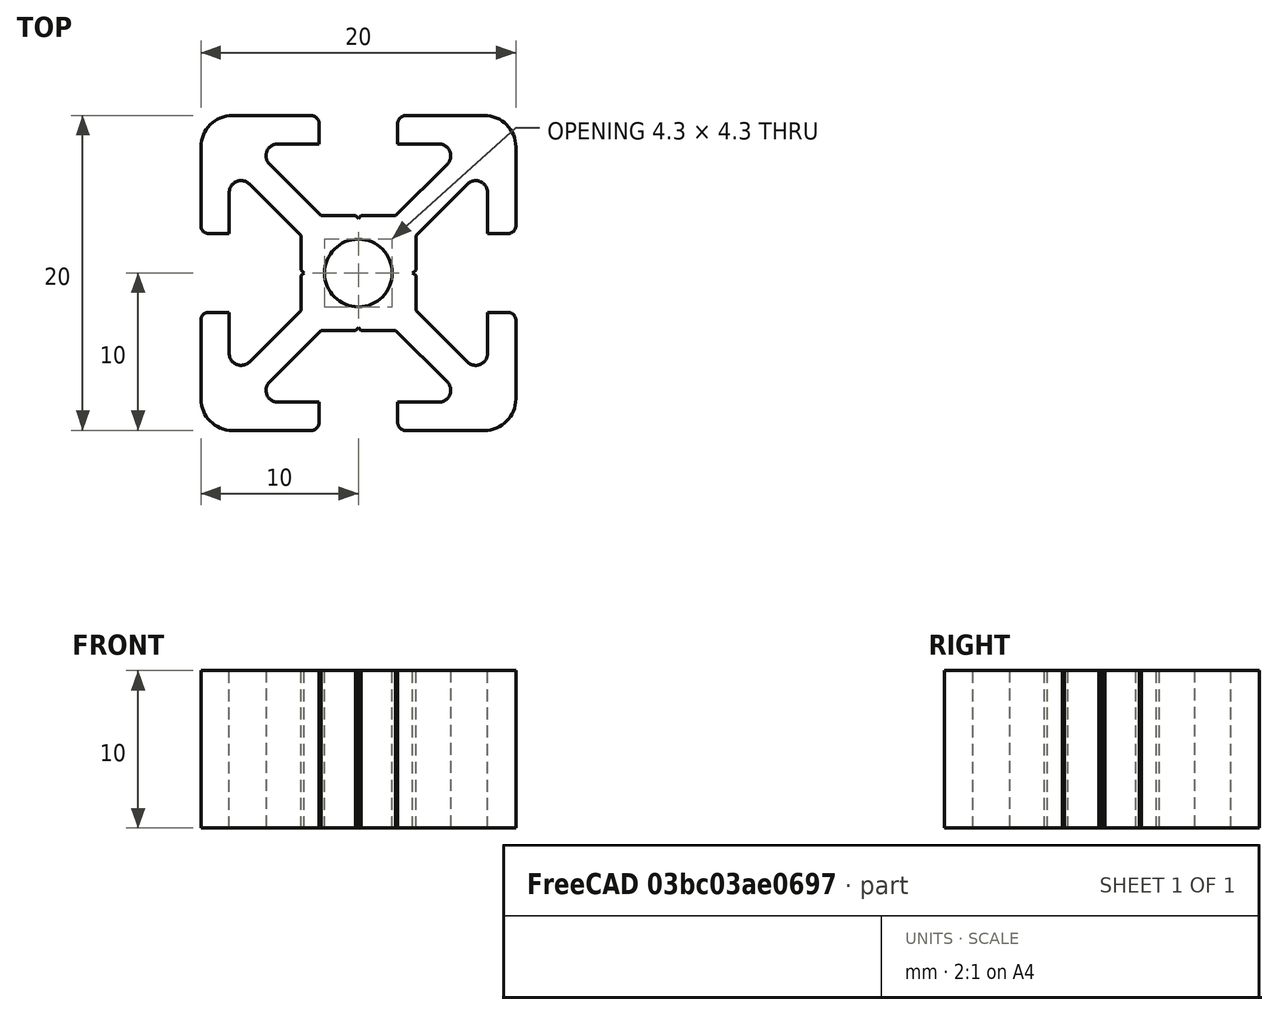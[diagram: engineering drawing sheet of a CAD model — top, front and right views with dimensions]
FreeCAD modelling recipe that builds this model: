
FCSTD DOCUMENT  (FreeCAD 0.18R)
Label: Profile-20x20-I-Type_Slot5
Comment: Item Compatible Profile\nLook for ISP5-L20
License: All rights reserved
LicenseURL: http://en.wikipedia.org/wiki/All_rights_reserved
objects: Sketcher::SketchObject×1, PartDesign::Pad×1, PartDesign::Body×1
note: 4 computed .brp shape members not serialized (recipe doc carries the construction recipe); baked Part::Feature solids carry a one-line shape summary decoded from their .brp

FEATURE [Sketcher::SketchObject] CopySketch029  label="ISP5-L20-Profile"
  MapMode = 5
  sketch-geometry (92):
    g0: LineSegment StartX=-2.37721 StartY=3.65 StartZ=0 EndX=-5.64688 EndY=6.91967 EndZ=0
    g1: LineSegment StartX=-5.11655 StartY=8.2 StartZ=0 EndX=-2.5 EndY=8.2 EndZ=0
    g2: LineSegment StartX=-3 StartY=10 StartZ=0 EndX=-8 EndY=10 EndZ=0
    g3: LineSegment StartX=-10 StartY=8 StartZ=0 EndX=-10 EndY=3 EndZ=0
    g4: LineSegment StartX=-9.5 StartY=2.5 StartZ=0 EndX=-8.2 EndY=2.5 EndZ=0
    g5: LineSegment StartX=-8.2 StartY=2.5 StartZ=0 EndX=-8.2 EndY=5.11655 EndZ=0
    g6: LineSegment StartX=-6.91967 StartY=5.64688 StartZ=0 EndX=-3.65 EndY=2.37721 EndZ=0
    g7: LineSegment StartX=-3.65 StartY=2.37721 StartZ=0 EndX=-3.65 EndY=0.177208 EndZ=0
    g8: LineSegment StartX=-0.177208 StartY=3.65 StartZ=0 EndX=-2.37721 EndY=3.65 EndZ=0
    g9: LineSegment StartX=-2.5 StartY=9.5 StartZ=0 EndX=-2.5 EndY=8.2 EndZ=0
    g10: LineSegment [constr] StartX=-8 StartY=8 StartZ=0 EndX=-9e-16 EndY=0 EndZ=0
    g11: LineSegment [constr] StartX=-3.65 StartY=2.37721 StartZ=0 EndX=-2.37721 EndY=3.65 EndZ=0
    g12: ArcOfCircle CenterX=-8 CenterY=8 CenterZ=0 NormalX=0 NormalY=0 NormalZ=1 AngleXU=0 Radius=2 StartAngle=1.5708 EndAngle=3.14159
    g13: ArcOfCircle CenterX=-3 CenterY=9.5 CenterZ=0 NormalX=0 NormalY=0 NormalZ=1 AngleXU=0 Radius=0.5 StartAngle=7e-16 EndAngle=1.5708
    g14: ArcOfCircle CenterX=-9.5 CenterY=3 CenterZ=0 NormalX=0 NormalY=0 NormalZ=1 AngleXU=0 Radius=0.5 StartAngle=3.14159 EndAngle=4.71239
    g15: ArcOfCircle CenterX=-5.11655 CenterY=7.45 CenterZ=0 NormalX=0 NormalY=0 NormalZ=1 AngleXU=0 Radius=0.75 StartAngle=1.5708 EndAngle=3.92699
    g16: ArcOfCircle CenterX=-7.45 CenterY=5.11655 CenterZ=0 NormalX=0 NormalY=0 NormalZ=1 AngleXU=0 Radius=0.75 StartAngle=0.785398 EndAngle=3.14159
    g17: LineSegment [constr] StartX=-5.11655 StartY=7.45 StartZ=0 EndX=-7.45 EndY=5.11655 EndZ=0
    g18: ArcOfCircle CenterX=-9e-16 CenterY=0 CenterZ=0 NormalX=0 NormalY=0 NormalZ=1 AngleXU=0 Radius=2.15 StartAngle=1.5708 EndAngle=3.14159
    g19: LineSegment StartX=1e-16 StartY=3.45 StartZ=0 EndX=1e-16 EndY=2.15 EndZ=0
    g20: LineSegment StartX=-3.45 StartY=3e-16 StartZ=0 EndX=-2.15 EndY=3e-16 EndZ=0
    g21: LineSegment StartX=-0.177208 StartY=3.65 StartZ=0 EndX=1e-16 EndY=3.45 EndZ=0
    g22: LineSegment StartX=-3.65 StartY=0.177208 StartZ=0 EndX=-3.45 EndY=3e-16 EndZ=0
    g23: LineSegment StartX=2.37721 StartY=3.65 StartZ=0 EndX=5.64688 EndY=6.91967 EndZ=0
    g24: LineSegment StartX=5.11655 StartY=8.2 StartZ=0 EndX=2.5 EndY=8.2 EndZ=0
    g25: LineSegment StartX=3 StartY=10 StartZ=0 EndX=8 EndY=10 EndZ=0
    g26: LineSegment StartX=10 StartY=8 StartZ=0 EndX=10 EndY=3 EndZ=0
    g27: LineSegment StartX=9.5 StartY=2.5 StartZ=0 EndX=8.2 EndY=2.5 EndZ=0
    g28: LineSegment StartX=8.2 StartY=2.5 StartZ=0 EndX=8.2 EndY=5.11655 EndZ=0
    g29: LineSegment StartX=6.91967 StartY=5.64688 StartZ=0 EndX=3.65 EndY=2.37721 EndZ=0
    g30: LineSegment StartX=3.65 StartY=2.37721 StartZ=0 EndX=3.65 EndY=0.177208 EndZ=0
    g31: LineSegment StartX=0.177208 StartY=3.65 StartZ=0 EndX=2.37721 EndY=3.65 EndZ=0
    g32: LineSegment StartX=2.5 StartY=9.5 StartZ=0 EndX=2.5 EndY=8.2 EndZ=0
    g33: LineSegment [constr] StartX=8 StartY=8 StartZ=0 EndX=9e-16 EndY=0 EndZ=0
    g34: LineSegment [constr] StartX=3.65 StartY=2.37721 StartZ=0 EndX=2.37721 EndY=3.65 EndZ=0
    g35: ArcOfCircle CenterX=8 CenterY=8 CenterZ=0 NormalX=0 NormalY=0 NormalZ=1 AngleXU=0 Radius=2 StartAngle=0 EndAngle=1.5708
    g36: ArcOfCircle CenterX=3 CenterY=9.5 CenterZ=0 NormalX=0 NormalY=0 NormalZ=1 AngleXU=0 Radius=0.5 StartAngle=1.5708 EndAngle=3.14159
    g37: ArcOfCircle CenterX=9.5 CenterY=3 CenterZ=0 NormalX=0 NormalY=0 NormalZ=1 AngleXU=0 Radius=0.5 StartAngle=4.71239 EndAngle=6.28319
    g38: ArcOfCircle CenterX=5.11655 CenterY=7.45 CenterZ=0 NormalX=0 NormalY=0 NormalZ=1 AngleXU=0 Radius=0.75 StartAngle=5.49779 EndAngle=7.85398
    g39: ArcOfCircle CenterX=7.45 CenterY=5.11655 CenterZ=0 NormalX=0 NormalY=0 NormalZ=1 AngleXU=0 Radius=0.75 StartAngle=0 EndAngle=2.35619
    g40: LineSegment [constr] StartX=5.11655 StartY=7.45 StartZ=0 EndX=7.45 EndY=5.11655 EndZ=0
    g41: ArcOfCircle CenterX=9e-16 CenterY=0 CenterZ=0 NormalX=0 NormalY=0 NormalZ=1 AngleXU=0 Radius=2.15 StartAngle=1e-16 EndAngle=1.5708
    g42: LineSegment StartX=5e-16 StartY=3.45 StartZ=0 EndX=5e-16 EndY=2.15 EndZ=0
    g43: LineSegment StartX=3.45 StartY=3e-16 StartZ=0 EndX=2.15 EndY=3e-16 EndZ=0
    g44: LineSegment StartX=0.177208 StartY=3.65 StartZ=0 EndX=5e-16 EndY=3.45 EndZ=0
    g45: LineSegment StartX=3.65 StartY=0.177208 StartZ=0 EndX=3.45 EndY=3e-16 EndZ=0
    g46: LineSegment StartX=-2.37721 StartY=-3.65 StartZ=0 EndX=-5.64688 EndY=-6.91967 EndZ=0
    g47: LineSegment StartX=-5.11655 StartY=-8.2 StartZ=0 EndX=-2.5 EndY=-8.2 EndZ=0
    g48: LineSegment StartX=-3 StartY=-10 StartZ=0 EndX=-8 EndY=-10 EndZ=0
    g49: LineSegment StartX=-10 StartY=-8 StartZ=0 EndX=-10 EndY=-3 EndZ=0
    g50: LineSegment StartX=-9.5 StartY=-2.5 StartZ=0 EndX=-8.2 EndY=-2.5 EndZ=0
    g51: LineSegment StartX=-8.2 StartY=-2.5 StartZ=0 EndX=-8.2 EndY=-5.11655 EndZ=0
    g52: LineSegment StartX=-6.91967 StartY=-5.64688 StartZ=0 EndX=-3.65 EndY=-2.37721 EndZ=0
    g53: LineSegment StartX=-3.65 StartY=-2.37721 StartZ=0 EndX=-3.65 EndY=-0.177208 EndZ=0
    g54: LineSegment StartX=-0.177208 StartY=-3.65 StartZ=0 EndX=-2.37721 EndY=-3.65 EndZ=0
    g55: LineSegment StartX=-2.5 StartY=-9.5 StartZ=0 EndX=-2.5 EndY=-8.2 EndZ=0
    g56: LineSegment [constr] StartX=-8 StartY=-8 StartZ=0 EndX=-9e-16 EndY=0 EndZ=0
    g57: LineSegment [constr] StartX=-3.65 StartY=-2.37721 StartZ=0 EndX=-2.37721 EndY=-3.65 EndZ=0
    g58: ArcOfCircle CenterX=-8 CenterY=-8 CenterZ=0 NormalX=0 NormalY=0 NormalZ=1 AngleXU=0 Radius=2 StartAngle=3.14159 EndAngle=4.71239
    g59: ArcOfCircle CenterX=-3 CenterY=-9.5 CenterZ=0 NormalX=0 NormalY=0 NormalZ=1 AngleXU=0 Radius=0.5 StartAngle=4.71239 EndAngle=6.28319
    g60: ArcOfCircle CenterX=-9.5 CenterY=-3 CenterZ=0 NormalX=0 NormalY=0 NormalZ=1 AngleXU=0 Radius=0.5 StartAngle=1.5708 EndAngle=3.14159
    g61: ArcOfCircle CenterX=-5.11655 CenterY=-7.45 CenterZ=0 NormalX=0 NormalY=0 NormalZ=1 AngleXU=0 Radius=0.75 StartAngle=2.35619 EndAngle=4.71239
    g62: ArcOfCircle CenterX=-7.45 CenterY=-5.11655 CenterZ=0 NormalX=0 NormalY=0 NormalZ=1 AngleXU=0 Radius=0.75 StartAngle=3.14159 EndAngle=5.49779
    g63: LineSegment [constr] StartX=-5.11655 StartY=-7.45 StartZ=0 EndX=-7.45 EndY=-5.11655 EndZ=0
    g64: ArcOfCircle CenterX=-9e-16 CenterY=0 CenterZ=0 NormalX=0 NormalY=0 NormalZ=1 AngleXU=0 Radius=2.15 StartAngle=3.14159 EndAngle=4.71239
    g65: LineSegment StartX=1e-16 StartY=-3.45 StartZ=0 EndX=1e-16 EndY=-2.15 EndZ=0
    g66: LineSegment StartX=-3.45 StartY=3e-16 StartZ=0 EndX=-2.15 EndY=3e-16 EndZ=0
    g67: LineSegment StartX=-0.177208 StartY=-3.65 StartZ=0 EndX=1e-16 EndY=-3.45 EndZ=0
    g68: LineSegment StartX=-3.65 StartY=-0.177208 StartZ=0 EndX=-3.45 EndY=3e-16 EndZ=0
    g69: LineSegment StartX=2.37721 StartY=-3.65 StartZ=0 EndX=5.64688 EndY=-6.91967 EndZ=0
    g70: LineSegment StartX=5.11655 StartY=-8.2 StartZ=0 EndX=2.5 EndY=-8.2 EndZ=0
    g71: LineSegment StartX=3 StartY=-10 StartZ=0 EndX=8 EndY=-10 EndZ=0
    g72: LineSegment StartX=10 StartY=-8 StartZ=0 EndX=10 EndY=-3 EndZ=0
    g73: LineSegment StartX=9.5 StartY=-2.5 StartZ=0 EndX=8.2 EndY=-2.5 EndZ=0
    g74: LineSegment StartX=8.2 StartY=-2.5 StartZ=0 EndX=8.2 EndY=-5.11655 EndZ=0
    g75: LineSegment StartX=6.91967 StartY=-5.64688 StartZ=0 EndX=3.65 EndY=-2.37721 EndZ=0
    g76: LineSegment StartX=3.65 StartY=-2.37721 StartZ=0 EndX=3.65 EndY=-0.177208 EndZ=0
    g77: LineSegment StartX=0.177208 StartY=-3.65 StartZ=0 EndX=2.37721 EndY=-3.65 EndZ=0
    g78: LineSegment StartX=2.5 StartY=-9.5 StartZ=0 EndX=2.5 EndY=-8.2 EndZ=0
    g79: LineSegment [constr] StartX=8 StartY=-8 StartZ=0 EndX=9e-16 EndY=0 EndZ=0
    g80: LineSegment [constr] StartX=3.65 StartY=-2.37721 StartZ=0 EndX=2.37721 EndY=-3.65 EndZ=0
    g81: ArcOfCircle CenterX=8 CenterY=-8 CenterZ=0 NormalX=0 NormalY=0 NormalZ=1 AngleXU=0 Radius=2 StartAngle=4.71239 EndAngle=6.28319
    g82: ArcOfCircle CenterX=3 CenterY=-9.5 CenterZ=0 NormalX=0 NormalY=0 NormalZ=1 AngleXU=0 Radius=0.5 StartAngle=3.14159 EndAngle=4.71239
    g83: ArcOfCircle CenterX=9.5 CenterY=-3 CenterZ=0 NormalX=0 NormalY=0 NormalZ=1 AngleXU=0 Radius=0.5 StartAngle=0 EndAngle=1.5708
    g84: ArcOfCircle CenterX=5.11655 CenterY=-7.45 CenterZ=0 NormalX=0 NormalY=0 NormalZ=1 AngleXU=0 Radius=0.75 StartAngle=4.71239 EndAngle=7.06858
    g85: ArcOfCircle CenterX=7.45 CenterY=-5.11655 CenterZ=0 NormalX=0 NormalY=0 NormalZ=1 AngleXU=0 Radius=0.75 StartAngle=3.92699 EndAngle=6.28319
    g86: LineSegment [constr] StartX=5.11655 StartY=-7.45 StartZ=0 EndX=7.45 EndY=-5.11655 EndZ=0
    g87: ArcOfCircle CenterX=9e-16 CenterY=0 CenterZ=0 NormalX=0 NormalY=0 NormalZ=1 AngleXU=0 Radius=2.15 StartAngle=4.71239 EndAngle=6.28319
    g88: LineSegment StartX=5e-16 StartY=-3.45 StartZ=0 EndX=5e-16 EndY=-2.15 EndZ=0
    g89: LineSegment StartX=3.45 StartY=-5e-16 StartZ=0 EndX=2.15 EndY=-5e-16 EndZ=0
    g90: LineSegment StartX=0.177208 StartY=-3.65 StartZ=0 EndX=5e-16 EndY=-3.45 EndZ=0
    g91: LineSegment StartX=3.65 StartY=-0.177208 StartZ=0 EndX=3.45 EndY=-5e-16 EndZ=0
  constraints (218):
    c: Coincident(g4,g5)
    c: Horizontal(g8)
    c: Vertical(g7)
    c: Horizontal(g2)
    c: Vertical(g3)
    c: Coincident(g1,g9)
    c: Vertical(g9)
    c: Horizontal(g1)
    c: Vertical(g5)
    c: Symmetric(g6,g0,g10)
    c: Parallel(g6,g10)
    c: Parallel(g10,g0)
    c: Coincident(g6,g11)
    c: Coincident(g11,g0)
    c: Coincident(g8,g0)
    c: Coincident(g7,g6)
    c: Radius(g12) = 2
    c: Horizontal(g4)
    c: Distance(g11) = 1.8
    c: Coincident(g2,g13)
    c: Coincident(g13,g9)
    c: Radius(g13) = 0.5
    c: DistanceY(g1,g2) = 1.8
    c: Coincident(g3,g14)
    c: Coincident(g14,g4)
    c: Radius(g14) = 0.5
    c: DistanceX(g3,g4) = 1.8
    c: Horizontal(g13,g9)
    c: Vertical(g2,g13)
    c: Coincident(g0,g15)
    c: Coincident(g15,g1)
    c: Vertical(g1,g15)
    c: Radius(g15) = 0.75
    c: Coincident(g16,g6)
    c: Coincident(g16,g5)
    c: Equal(g15,g16)
    c: Horizontal(g5,g16)
    c: Coincident(g16,g17)
    c: Coincident(g15,g17)
    c: PointOnObject(g0,g17)
    c: PointOnObject(g6,g17)
    c: Coincident(g10,g12)
    c: Tangent(g12,g2) = -1.5708
    c: Tangent(g12,g3) = -1.5708
    c: Horizontal(g3,g14)
    c: Vertical(g14,g4)
    c: Radius(g18) = 2.15
    c: PointOnObject(g18,g-2)
    c: PointOnObject(g18,g-1)
    c: Coincident(g18,g20)
    c: Coincident(g18,g19)
    c: Vertical(g19)
    c: Horizontal(g20)
    c: Coincident(g18,g10)
    c: Coincident(g-1,g18)
    c: Angle(g-1,g10) = 2.35619
    c: DistanceX(g3,g18) = 10
    c: DistanceY(g18,g4) = 2.5
    c: DistanceX(g1,g18) = 2.5
    c: Coincident(g19,g21)
    c: Coincident(g8,g21)
    c: DistanceX(g8,g8) = 2.2
    c: Coincident(g20,g22)
    c: Coincident(g22,g7)
    c: Equal(g8,g7)
    c: Equal(g19,g20)
    c: DistanceY(g19,g8) = 0.2
    c: DistanceY(g8,g2) = 6.35
    c: Coincident(g27,g28)
    c: Horizontal(g31)
    c: Vertical(g30)
    c: Horizontal(g25)
    c: Vertical(g26)
    c: Coincident(g24,g32)
    c: Vertical(g32)
    c: Horizontal(g24)
    c: Vertical(g28)
    c: Symmetric(g29,g23,g33)
    c: Parallel(g29,g33)
    c: Parallel(g33,g23)
    c: Coincident(g29,g34)
    c: Coincident(g34,g23)
    c: Coincident(g31,g23)
    c: Coincident(g30,g29)
    c: Radius(g35) = 2
    c: Horizontal(g27)
    c: Distance(g34) = 1.8
    c: Coincident(g25,g36)
    c: Coincident(g36,g32)
    c: Radius(g36) = 0.5
    c: Coincident(g26,g37)
    c: Coincident(g37,g27)
    c: Radius(g37) = 0.5
    c: Coincident(g23,g38)
    c: Coincident(g38,g24)
    c: Radius(g38) = 0.75
    c: Coincident(g39,g29)
    c: Coincident(g39,g28)
    c: Equal(g38,g39)
    c: Coincident(g39,g40)
    c: Coincident(g38,g40)
    c: PointOnObject(g23,g40)
    c: PointOnObject(g29,g40)
    c: Coincident(g33,g35)
    c: Tangent(g35,g25) = 1.5708
    c: Tangent(g35,g26) = 1.5708
    c: Radius(g41) = 2.15
    c: Coincident(g41,g43)
    c: Coincident(g41,g42)
    c: Vertical(g42)
    c: Horizontal(g43)
    c: Coincident(g41,g33)
    c: Coincident(g42,g44)
    c: Coincident(g31,g44)
    c: Coincident(g43,g45)
    c: Coincident(g45,g30)
    c: Equal(g31,g30)
    c: Equal(g42,g43)
    c: Coincident(g50,g51)
    c: Horizontal(g54)
    c: Vertical(g53)
    c: Horizontal(g48)
    c: Vertical(g49)
    c: Coincident(g47,g55)
    c: Vertical(g55)
    c: Horizontal(g47)
    c: Vertical(g51)
    c: Symmetric(g52,g46,g56)
    c: Parallel(g52,g56)
    c: Parallel(g56,g46)
    c: Coincident(g52,g57)
    c: Coincident(g57,g46)
    c: Coincident(g54,g46)
    c: Coincident(g53,g52)
    c: Radius(g58) = 2
    c: Horizontal(g50)
    c: Distance(g57) = 1.8
    c: Coincident(g48,g59)
    c: Coincident(g59,g55)
    c: Radius(g59) = 0.5
    c: Coincident(g49,g60)
    c: Coincident(g60,g50)
    c: Radius(g60) = 0.5
    c: Coincident(g46,g61)
    c: Coincident(g61,g47)
    c: Radius(g61) = 0.75
    c: Coincident(g62,g52)
    c: Coincident(g62,g51)
    c: Equal(g61,g62)
    c: Coincident(g62,g63)
    c: Coincident(g61,g63)
    c: PointOnObject(g46,g63)
    c: PointOnObject(g52,g63)
    c: Coincident(g56,g58)
    c: Tangent(g58,g48) = 1.5708
    c: Tangent(g58,g49) = 1.5708
    c: Radius(g64) = 2.15
    c: Coincident(g64,g66)
    c: Coincident(g64,g65)
    c: Vertical(g65)
    c: Horizontal(g66)
    c: Coincident(g64,g56)
    c: Coincident(g65,g67)
    c: Coincident(g54,g67)
    c: Coincident(g66,g68)
    c: Coincident(g68,g53)
    c: Equal(g54,g53)
    c: Equal(g65,g66)
    c: Coincident(g73,g74)
    c: Horizontal(g77)
    c: Vertical(g76)
    c: Horizontal(g71)
    c: Vertical(g72)
    c: Coincident(g70,g78)
    c: Vertical(g78)
    c: Horizontal(g70)
    c: Vertical(g74)
    c: Symmetric(g75,g69,g79)
    c: Parallel(g75,g79)
    c: Parallel(g79,g69)
    c: Coincident(g75,g80)
    c: Coincident(g80,g69)
    c: Coincident(g77,g69)
    c: Coincident(g76,g75)
    c: Radius(g81) = 2
    c: Horizontal(g73)
    c: Distance(g80) = 1.8
    c: Coincident(g71,g82)
    c: Coincident(g82,g78)
    c: Radius(g82) = 0.5
    c: Coincident(g72,g83)
    c: Coincident(g83,g73)
    c: Radius(g83) = 0.5
    c: Coincident(g69,g84)
    c: Coincident(g84,g70)
    c: Radius(g84) = 0.75
    c: Coincident(g85,g75)
    c: Coincident(g85,g74)
    c: Equal(g84,g85)
    c: Coincident(g85,g86)
    c: Coincident(g84,g86)
    c: PointOnObject(g69,g86)
    c: PointOnObject(g75,g86)
    c: Coincident(g79,g81)
    c: Tangent(g81,g71) = -1.5708
    c: Tangent(g81,g72) = -1.5708
    c: Radius(g87) = 2.15
    c: Coincident(g87,g89)
    c: Coincident(g87,g88)
    c: Vertical(g88)
    c: Horizontal(g89)
    c: Coincident(g87,g79)
    c: Coincident(g88,g90)
    c: Coincident(g77,g90)
    c: Coincident(g89,g91)
    c: Coincident(g91,g76)
    c: Equal(g77,g76)
    c: Equal(g88,g89)
FEATURE [PartDesign::Pad] Pad
  Length = 10
  Length2 = 100
  Profile = -> CopySketch029
  Type = 0
FEATURE [PartDesign::Body] Body
  Group = -> [CopySketch029,Pad]
  Origin = -> Origin
  Tip = -> Pad
